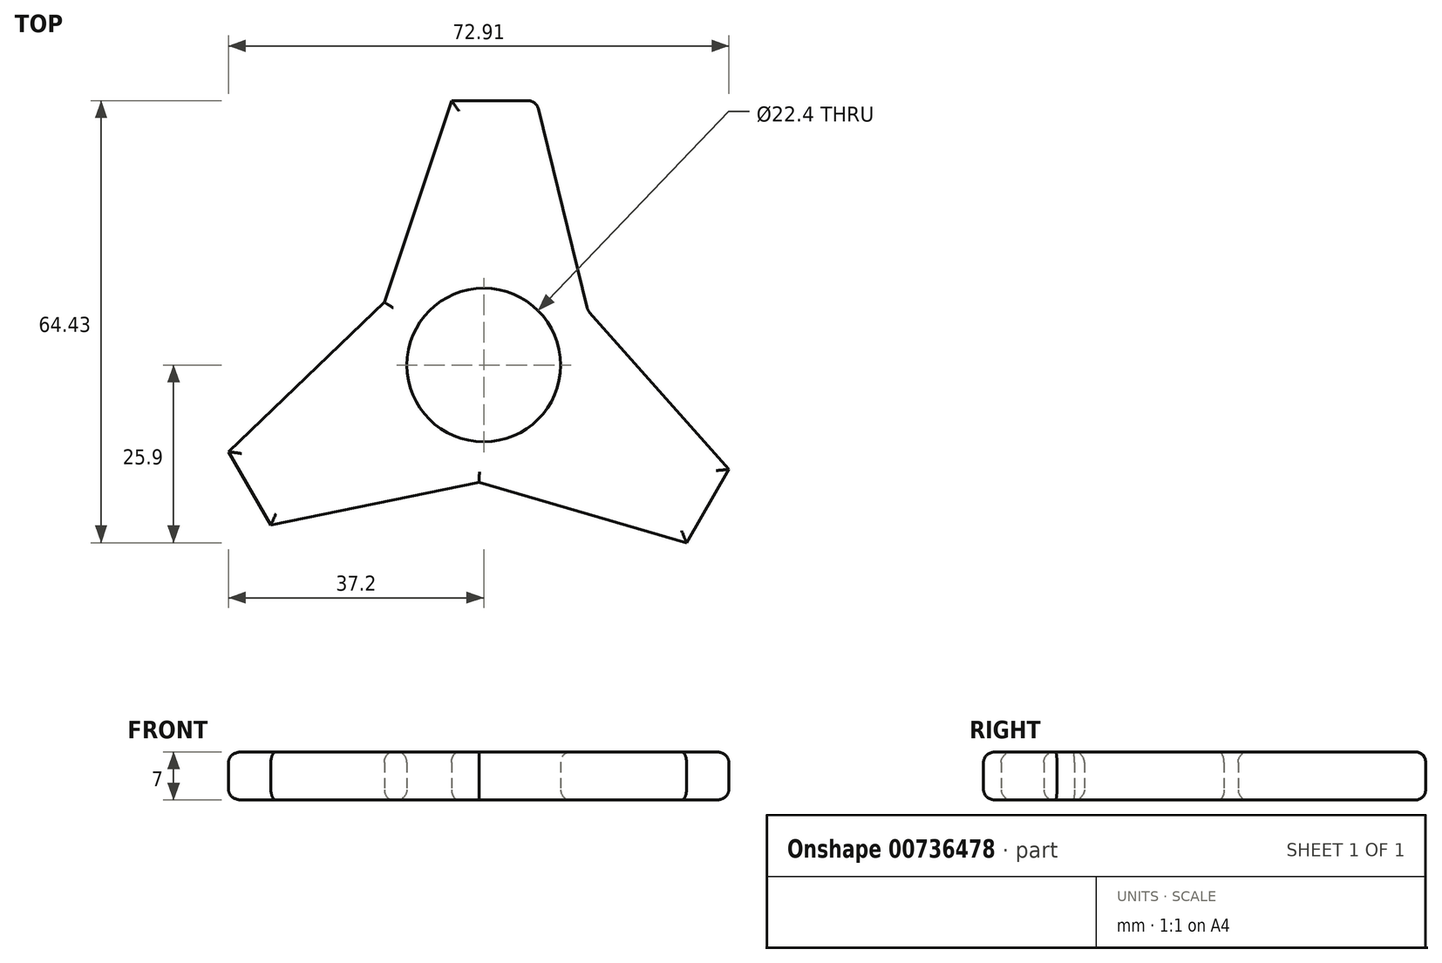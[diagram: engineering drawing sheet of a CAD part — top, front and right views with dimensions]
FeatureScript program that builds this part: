
annotation { "Feature Type Name" : "Feature", "Feature Type Description" : "" }
export const myFeature = defineFeature(function(context is Context, id is Id, definition is map)
    precondition{}
    {
        {
            var Q0;
            Q0=qCreatedBy(makeId("Top.planeOp"),FACE);
            var sketch = newSketch(context, id + "F0", { "sketchPlane" : qUnion([Q0])});
            skCircle(sketch, "E0", {"center": v(0, 0) * mm, "radius": 11.2 * mm});
            skLineSegment(sketch, "E1", {"start": v(-14.48, 9.16) * mm, "end": v(-4.7, 38.53) * mm});
            skLineSegment(sketch, "E2", {"start": v(-4.7, 38.53) * mm, "end": v(7.66, 38.53) * mm});
            skLineSegment(sketch, "E3", {"start": v(7.66, 38.53) * mm, "end": v(15.17, 7.96) * mm});
            skLineSegment(sketch, "E4.1.0", {"start": v(-31.02, -23.33) * mm, "end": v(-37.2, -12.63) * mm});
            skLineSegment(sketch, "E4.1.1", {"start": v(-37.2, -12.63) * mm, "end": v(-14.48, 9.16) * mm});
            skLineSegment(sketch, "E4.1.2", {"start": v(-0.7, -17.12) * mm, "end": v(-31.02, -23.33) * mm});
            skLineSegment(sketch, "E4.2.0", {"start": v(35.71, -15.2) * mm, "end": v(29.54, -25.9) * mm});
            skLineSegment(sketch, "E4.2.1", {"start": v(29.54, -25.9) * mm, "end": v(-0.7, -17.12) * mm});
            skLineSegment(sketch, "E4.2.2", {"start": v(15.17, 7.96) * mm, "end": v(35.71, -15.2) * mm});
            skPoint(sketch, "E5.orphan", {"position": v(-15.78, 5.26) * mm});
            skPoint(sketch, "E6.orphan", {"position": v(-11.51, 12) * mm});
            skPoint(sketch, "E7.orphan", {"position": v(12.44, 11.04) * mm});
            skPoint(sketch, "E8.orphan", {"position": v(16.15, 3.97) * mm});
            skPoint(sketch, "E9.orphan", {"position": v(3.34, -16.3) * mm});
            skSolve(sketch);
        }
        {
            var Q0;
            Q0=makeQuery(id+"F0.imprint","IMPRINT",FACE,{"disambiguationData":[TD([[makeQuery(id+"F0.imprint","IMPRINT",EDGE,{"derivedFrom":sQuery(id+"F0.wireOp",EDGE,"E0")}),-1.0]])]});
            extrude(context, id + "F1", {"entities" : qUnion([Q0]), "depth" : 7 * mm, "offsetDistance" : 25 * mm});
        }
        {
            var Q0;
            Q0=makeQuery(id+"F1.opExtrude","CAP_EDGE",EDGE,{"disambiguationData":[OSD([sQuery(id+"F0.wireOp",EDGE,"E1")])],"isStart":false});
            var Q1;
            Q1=makeQuery(id+"F1.opExtrude","CAP_EDGE",EDGE,{"disambiguationData":[OSD([sQuery(id+"F0.wireOp",EDGE,"E4.1.1")])],"isStart":false});
            var Q2;
            Q2=makeQuery(id+"F1.opExtrude","CAP_EDGE",EDGE,{"disambiguationData":[OSD([sQuery(id+"F0.wireOp",EDGE,"E4.1.0")])],"isStart":false});
            var Q3;
            Q3=makeQuery(id+"F1.opExtrude","CAP_FACE",FACE,{"disambiguationData":[OSD([sQuery(id+"F0.wireOp",EDGE,"E0"),sQuery(id+"F0.wireOp",EDGE,"E1"),sQuery(id+"F0.wireOp",EDGE,"E2"),sQuery(id+"F0.wireOp",EDGE,"E3"),sQuery(id+"F0.wireOp",EDGE,"E4.1.0"),sQuery(id+"F0.wireOp",EDGE,"E4.1.1"),sQuery(id+"F0.wireOp",EDGE,"E4.1.2"),sQuery(id+"F0.wireOp",EDGE,"E4.2.0"),sQuery(id+"F0.wireOp",EDGE,"E4.2.1"),sQuery(id+"F0.wireOp",EDGE,"E4.2.2")])],"isStart":false});
            var Q4;
            Q4=makeQuery(id+"F1.opExtrude","SWEPT_FACE",FACE,{"disambiguationData":[OSD([sQuery(id+"F0.wireOp",EDGE,"E3")])]});
            var Q5;
            Q5=makeQuery(id+"F1.opExtrude","CAP_FACE",FACE,{"disambiguationData":[OSD([sQuery(id+"F0.wireOp",EDGE,"E0"),sQuery(id+"F0.wireOp",EDGE,"E1"),sQuery(id+"F0.wireOp",EDGE,"E2"),sQuery(id+"F0.wireOp",EDGE,"E3"),sQuery(id+"F0.wireOp",EDGE,"E4.1.0"),sQuery(id+"F0.wireOp",EDGE,"E4.1.1"),sQuery(id+"F0.wireOp",EDGE,"E4.1.2"),sQuery(id+"F0.wireOp",EDGE,"E4.2.0"),sQuery(id+"F0.wireOp",EDGE,"E4.2.1"),sQuery(id+"F0.wireOp",EDGE,"E4.2.2")])],"isStart":true});
            fillet(context, id + "F2", {"entities" : qUnion([Q0, Q1, Q2, Q3, Q4, Q5]), "radius" : 1.5 * mm, "tangentPropagation" : true, "allowEdgeOverflow" : false});
        }
    });
